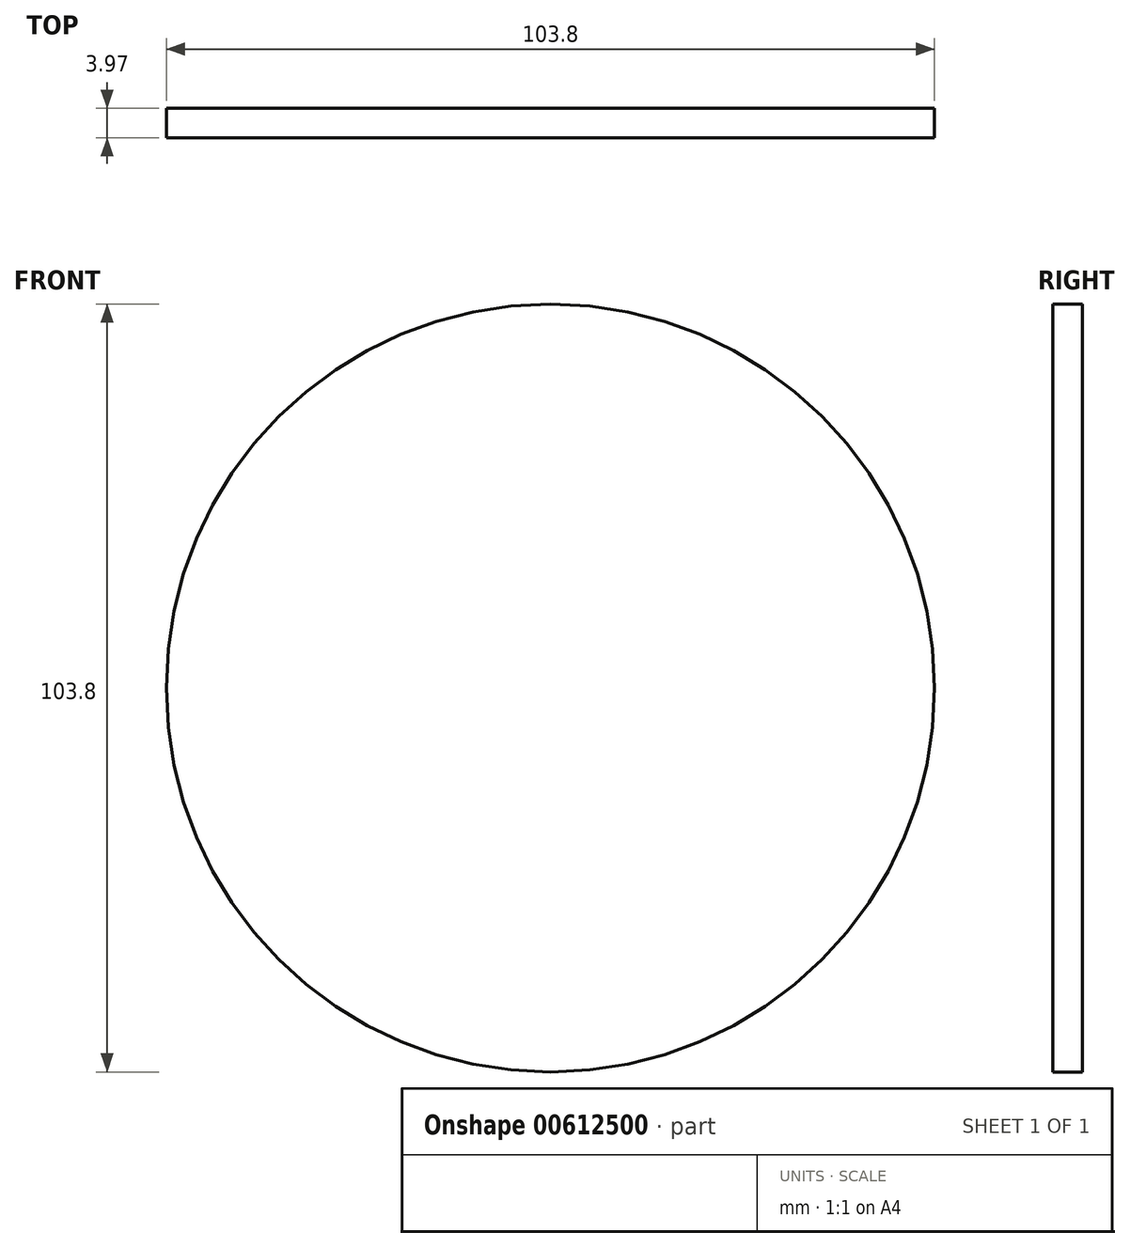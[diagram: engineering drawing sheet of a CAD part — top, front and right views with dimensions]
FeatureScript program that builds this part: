
annotation { "Feature Type Name" : "Feature", "Feature Type Description" : "" }
export const myFeature = defineFeature(function(context is Context, id is Id, definition is map)
    precondition{}
    {
        {
            var Q0;
            Q0=qCreatedBy(makeId("Front.planeOp"),FACE);
            var sketch = newSketch(context, id + "F0", { "sketchPlane" : qUnion([Q0])});
            skCircle(sketch, "E0", {"center": v(0, 0) * mm, "radius": 51.9 * mm});
            skSolve(sketch);
        }
        {
            var Q0;
            Q0=makeQuery(id+"F0.imprint","IMPRINT",FACE,{"disambiguationData":[TD([[makeQuery(id+"F0.imprint","IMPRINT",EDGE,{"derivedFrom":sQuery(id+"F0.wireOp",EDGE,"E0")}),1.0]])]});
            extrude(context, id + "F1", {"entities" : qUnion([Q0]), "depth" : 3.97 * mm, "offsetDistance" : 25.4 * mm});
        }
    });
